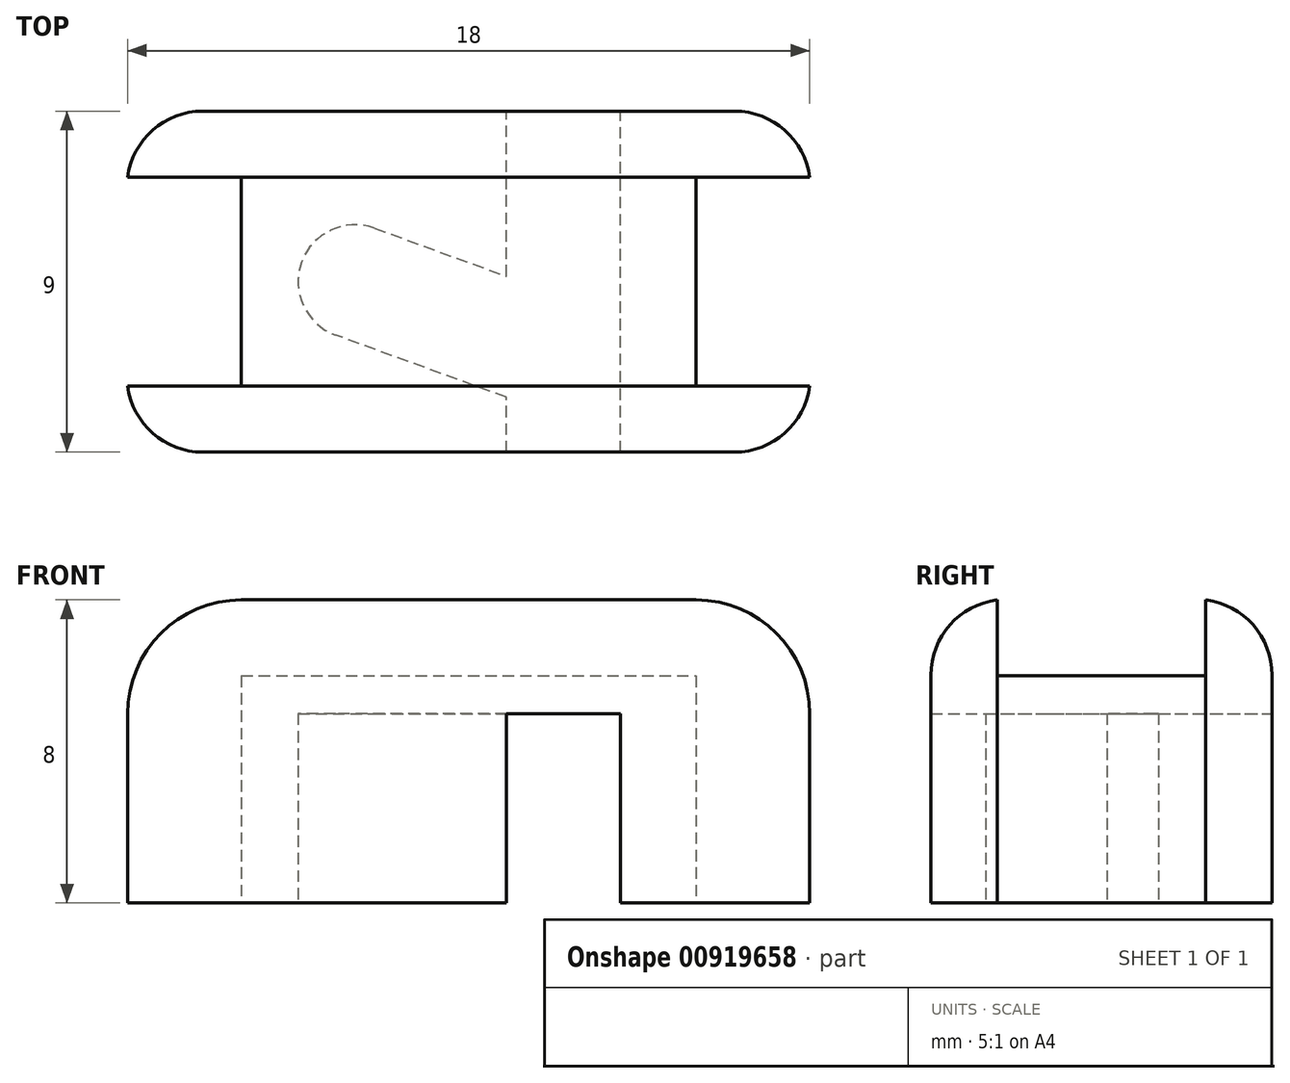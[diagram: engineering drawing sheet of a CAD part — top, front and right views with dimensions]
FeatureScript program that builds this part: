
annotation { "Feature Type Name" : "Feature", "Feature Type Description" : "" }
export const myFeature = defineFeature(function(context is Context, id is Id, definition is map)
    precondition{}
    {
        {
            var Q0;
            Q0=qCreatedBy(makeId("Front.planeOp"),FACE);
            var sketch = newSketch(context, id + "F0", { "sketchPlane" : qUnion([Q0])});
            skLineSegment(sketch, "E0.bottom", {"start": v(-6, 8) * mm, "end": v(6, 8) * mm});
            skLineSegment(sketch, "E0.top", {"start": v(-9, 0) * mm, "end": v(9, 0) * mm});
            skLineSegment(sketch, "E0.left", {"start": v(-9, 5) * mm, "end": v(-9, 0) * mm});
            skLineSegment(sketch, "E0.right", {"start": v(9, 5) * mm, "end": v(9, 0) * mm});
            skPoint(sketch, "E1.visualSharp", {"position": v(-9, 8) * mm});
            skArc(sketch, "E1.filletArc", {"start": v(-6, 8) * mm, "mid": v(-8.12, 7.12) * mm, "end": v(-9, 5) * mm});
            skPoint(sketch, "E2.visualSharp", {"position": v(9, 8) * mm});
            skArc(sketch, "E2.filletArc", {"start": v(9, 5) * mm, "mid": v(8.12, 7.12) * mm, "end": v(6, 8) * mm});
            skSolve(sketch);
        }
        {
            var Q0;
            Q0 = qSketchRegion(id + "F0", true);
            extrude(context, id + "F1", {"entities" : qUnion([Q0]), "endBound" : BoundingType.SYMMETRIC, "depth" : 9 * mm, "offsetDistance" : 25 * mm});
        }
        {
            var Q0;
            Q0=qCreatedBy(makeId("Front.planeOp"),FACE);
            var sketch = newSketch(context, id + "F2", { "sketchPlane" : qUnion([Q0])});
            skLineSegment(sketch, "E3.top", {"start": v(-24, 0) * mm, "end": v(-6, 0) * mm});
            skLineSegment(sketch, "E3.right", {"start": v(-6, 6) * mm, "end": v(-6, 0) * mm});
            skLineSegment(sketch, "E4.MirrorCS", {"start": v(6, 6) * mm, "end": v(6, 0) * mm});
            skLineSegment(sketch, "E5.MirrorCS", {"start": v(24, 0) * mm, "end": v(6, 0) * mm});
            skLineSegment(sketch, "E6", {"start": v(-6, 6) * mm, "end": v(6, 6) * mm});
            skLineSegment(sketch, "E7", {"start": v(-24, 0) * mm, "end": v(-24, 24) * mm});
            skLineSegment(sketch, "E8", {"start": v(-24, 24) * mm, "end": v(24, 24) * mm});
            skLineSegment(sketch, "E9", {"start": v(24, 24) * mm, "end": v(24, 0) * mm});
            skSolve(sketch);
        }
        {
            var Q0;
            Q0 = qSketchRegion(id + "F2", true);
            extrude(context, id + "F3", {"entities" : qUnion([Q0]), "operationType" : NewBodyOperationType.REMOVE, "endBound" : BoundingType.SYMMETRIC, "oppositeDirection" : true, "depth" : 5.5 * mm, "offsetDistance" : 25 * mm});
        }
        {
            var Q0;
            Q0=makeQuery(id+"F1.opExtrude","SWEPT_FACE",FACE,{"disambiguationData":[OSD([sQuery(id+"F0.wireOp",EDGE,"E0.top")])]});
            var sketch = newSketch(context, id + "F4", { "sketchPlane" : qUnion([Q0])});
            skCircle(sketch, "E10", {"center": v(-3, 0) * mm, "radius": 1.5 * mm, "construction": true});
            skLineSegment(sketch, "E11", {"start": v(4, 6) * mm, "end": v(1, 6) * mm});
            skLineSegment(sketch, "E12", {"start": v(1, 6) * mm, "end": v(1, 3.05) * mm});
            skLineSegment(sketch, "E13", {"start": v(1, 3.05) * mm, "end": v(-3.51, 1.4) * mm});
            skLineSegment(sketch, "E14.MirrorCS", {"start": v(4, -6) * mm, "end": v(1, -6) * mm});
            skLineSegment(sketch, "E15", {"start": v(4, 6) * mm, "end": v(4, -6) * mm});
            skLineSegment(sketch, "E16", {"start": v(-2.49, -1.4) * mm, "end": v(1, -0.14) * mm});
            skLineSegment(sketch, "E17", {"start": v(1, -0.14) * mm, "end": v(1, -6) * mm});
            skArc(sketch, "E18", {"start": v(-3.51, 1.4) * mm, "mid": v(-4.4, -0.51) * mm, "end": v(-2.49, -1.4) * mm});
            skSolve(sketch);
        }
        {
            var Q0;
            Q0 = qSketchRegion(id + "F4", true);
            extrude(context, id + "F5", {"entities" : qUnion([Q0]), "operationType" : NewBodyOperationType.REMOVE, "oppositeDirection" : true, "depth" : 5 * mm, "offsetDistance" : 25 * mm});
        }
        {
            var Q0;
            Q0=makeQuery(id+"F1.opExtrude","CAP_EDGE",EDGE,{"disambiguationData":[OSD([sQuery(id+"F0.wireOp",EDGE,"E1.filletArc")])],"isStart":false});
            var Q1;
            Q1=makeQuery(id+"F1.opExtrude","CAP_EDGE",EDGE,{"disambiguationData":[OSD([sQuery(id+"F0.wireOp",EDGE,"E2.filletArc")])],"isStart":true});
            fillet(context, id + "F6", {"entities" : qUnion([Q0, Q1]), "radius" : 2 * mm, "tangentPropagation" : true, "allowEdgeOverflow" : false});
        }
    });
